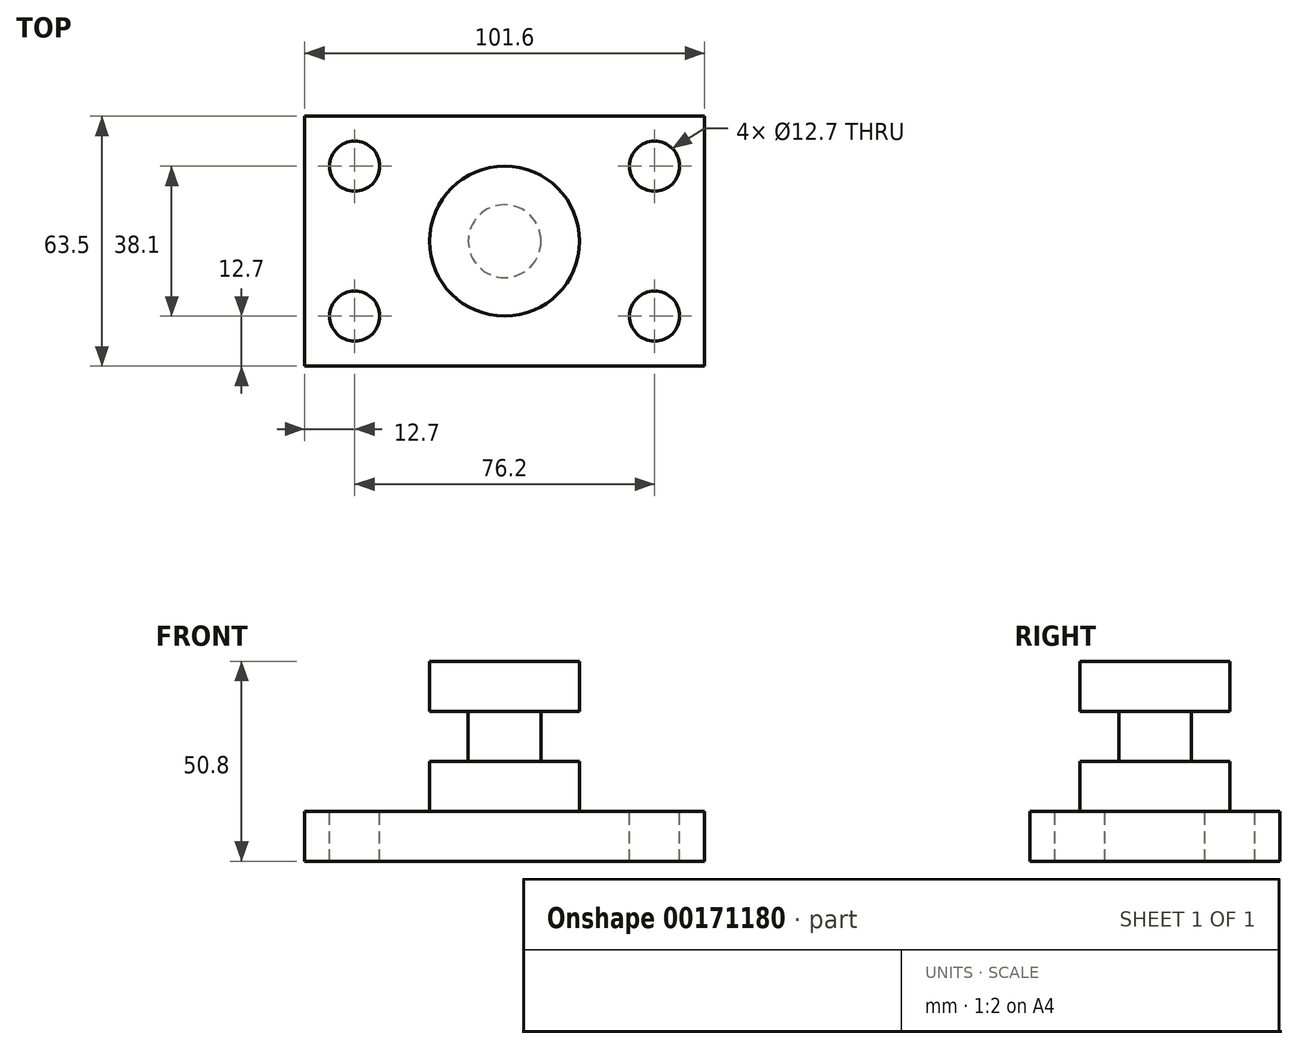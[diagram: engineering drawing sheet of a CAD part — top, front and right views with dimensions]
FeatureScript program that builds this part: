
annotation { "Feature Type Name" : "Feature", "Feature Type Description" : "" }
export const myFeature = defineFeature(function(context is Context, id is Id, definition is map)
    precondition{}
    {
        {
            var Q0;
            Q0=qCreatedBy(makeId("Top.planeOp"),FACE);
            var sketch = newSketch(context, id + "F0", { "sketchPlane" : qUnion([Q0])});
            skLineSegment(sketch, "E0.bottom", {"start": v(-50.8, 31.75) * mm, "end": v(50.8, 31.75) * mm});
            skLineSegment(sketch, "E0.top", {"start": v(-50.8, -31.75) * mm, "end": v(50.8, -31.75) * mm});
            skLineSegment(sketch, "E0.left", {"start": v(-50.8, 31.75) * mm, "end": v(-50.8, -31.75) * mm});
            skLineSegment(sketch, "E0.right", {"start": v(50.8, 31.75) * mm, "end": v(50.8, -31.75) * mm});
            skPoint(sketch, "E0.middle", {"position": v(0, 0) * mm});
            skSolve(sketch);
        }
        {
            var Q0;
            Q0=makeQuery(id+"F0.imprint","IMPRINT",FACE,{"disambiguationData":[TD([[makeQuery(id+"F0.imprint","IMPRINT",EDGE,{"derivedFrom":sQuery(id+"F0.wireOp",EDGE,"E0.bottom")}),-1.0]])]});
            extrude(context, id + "F1", {"entities" : qUnion([Q0]), "depth" : 12.7 * mm});
        }
        {
            var Q0;
            Q0=makeQuery(id+"F1.opExtrude","CAP_FACE",FACE,{"disambiguationData":[OSD([sQuery(id+"F0.wireOp",EDGE,"E0.bottom"),sQuery(id+"F0.wireOp",EDGE,"E0.top"),sQuery(id+"F0.wireOp",EDGE,"E0.left"),sQuery(id+"F0.wireOp",EDGE,"E0.right")])],"isStart":false});
            var sketch = newSketch(context, id + "F2", { "sketchPlane" : qUnion([Q0])});
            skCircle(sketch, "E1", {"center": v(38.1, 19.05) * mm, "radius": 6.35 * mm});
            skCircle(sketch, "E2", {"center": v(-38.1, 19.05) * mm, "radius": 6.35 * mm});
            skCircle(sketch, "E3", {"center": v(-38.1, -19.05) * mm, "radius": 6.35 * mm});
            skCircle(sketch, "E4", {"center": v(38.1, -19.05) * mm, "radius": 6.35 * mm});
            skSolve(sketch);
        }
        {
            var Q0;
            Q0=makeQuery(id+"F2.imprint","IMPRINT",FACE,{"disambiguationData":[TD([[makeQuery(id+"F2.imprint","IMPRINT",EDGE,{"derivedFrom":sQuery(id+"F2.wireOp",EDGE,"E3")}),1.0]])]});
            var Q1;
            Q1=makeQuery(id+"F2.imprint","IMPRINT",FACE,{"disambiguationData":[TD([[makeQuery(id+"F2.imprint","IMPRINT",EDGE,{"derivedFrom":sQuery(id+"F2.wireOp",EDGE,"E2")}),1.0]])]});
            var Q2;
            Q2=makeQuery(id+"F2.imprint","IMPRINT",FACE,{"disambiguationData":[TD([[makeQuery(id+"F2.imprint","IMPRINT",EDGE,{"derivedFrom":sQuery(id+"F2.wireOp",EDGE,"E4")}),1.0]])]});
            var Q3;
            Q3=makeQuery(id+"F2.imprint","IMPRINT",FACE,{"disambiguationData":[TD([[makeQuery(id+"F2.imprint","IMPRINT",EDGE,{"derivedFrom":sQuery(id+"F2.wireOp",EDGE,"E1")}),1.0]])]});
            extrude(context, id + "F3", {"entities" : qUnion([Q0, Q1, Q2, Q3]), "operationType" : NewBodyOperationType.REMOVE, "oppositeDirection" : true, "depth" : 25.4 * mm});
        }
        {
            var Q0;
            Q0=qCreatedBy(makeId("Front.planeOp"),FACE);
            var sketch = newSketch(context, id + "F4", { "sketchPlane" : qUnion([Q0])});
            skLineSegment(sketch, "E5.bottom", {"start": v(0, 12.7) * mm, "end": v(-19.05, 12.7) * mm});
            skLineSegment(sketch, "E5.top", {"start": v(0, 50.8) * mm, "end": v(-19.05, 50.8) * mm});
            skLineSegment(sketch, "E5.left", {"start": v(0, 12.7) * mm, "end": v(0, 50.8) * mm});
            skLineSegment(sketch, "E5.right", {"start": v(-19.05, 12.7) * mm, "end": v(-19.05, 50.8) * mm});
            skSolve(sketch);
        }
        {
            var Q0;
            Q0=makeQuery(id+"F4.imprint","IMPRINT",FACE,{"disambiguationData":[TD([[makeQuery(id+"F4.imprint","IMPRINT",EDGE,{"derivedFrom":sQuery(id+"F4.wireOp",EDGE,"E5.bottom")}),-1.0]])]});
            var Q1;
            Q1=sQuery(id+"F4.wireOp",EDGE,"E5.left");
            revolve(context, id + "F5", {"entities" : qUnion([Q0]), "axis" : qUnion([Q1]), "revolveType" : RevolveType.FULL});
        }
        {
            var Q0;
            Q0=qCreatedBy(makeId("Front.planeOp"),FACE);
            var sketch = newSketch(context, id + "F6", { "sketchPlane" : qUnion([Q0])});
            skLineSegment(sketch, "E6.bottom", {"start": v(-9.24, 38.1) * mm, "end": v(-45.56, 38.1) * mm});
            skLineSegment(sketch, "E6.top", {"start": v(-9.24, 25.4) * mm, "end": v(-45.56, 25.4) * mm});
            skLineSegment(sketch, "E6.left", {"start": v(-9.24, 38.1) * mm, "end": v(-9.24, 25.4) * mm});
            skLineSegment(sketch, "E6.right", {"start": v(-45.56, 38.1) * mm, "end": v(-45.56, 25.4) * mm});
            skLineSegment(sketch, "E7", {"start": v(0, 0) * mm, "end": v(0, 67.19) * mm});
            skSolve(sketch);
        }
        {
            var Q0;
            Q0=makeQuery(id+"F6.imprint","IMPRINT",FACE,{"disambiguationData":[TD([[makeQuery(id+"F6.imprint","IMPRINT",EDGE,{"derivedFrom":sQuery(id+"F6.wireOp",EDGE,"E6.bottom")}),1.0]])]});
            var Q1;
            Q1=sQuery(id+"F6.wireOp",EDGE,"E7");
            revolve(context, id + "F7", {"operationType" : NewBodyOperationType.REMOVE, "entities" : qUnion([Q0]), "axis" : qUnion([Q1]), "revolveType" : RevolveType.FULL, "oppositeDirection" : true});
        }
    });
